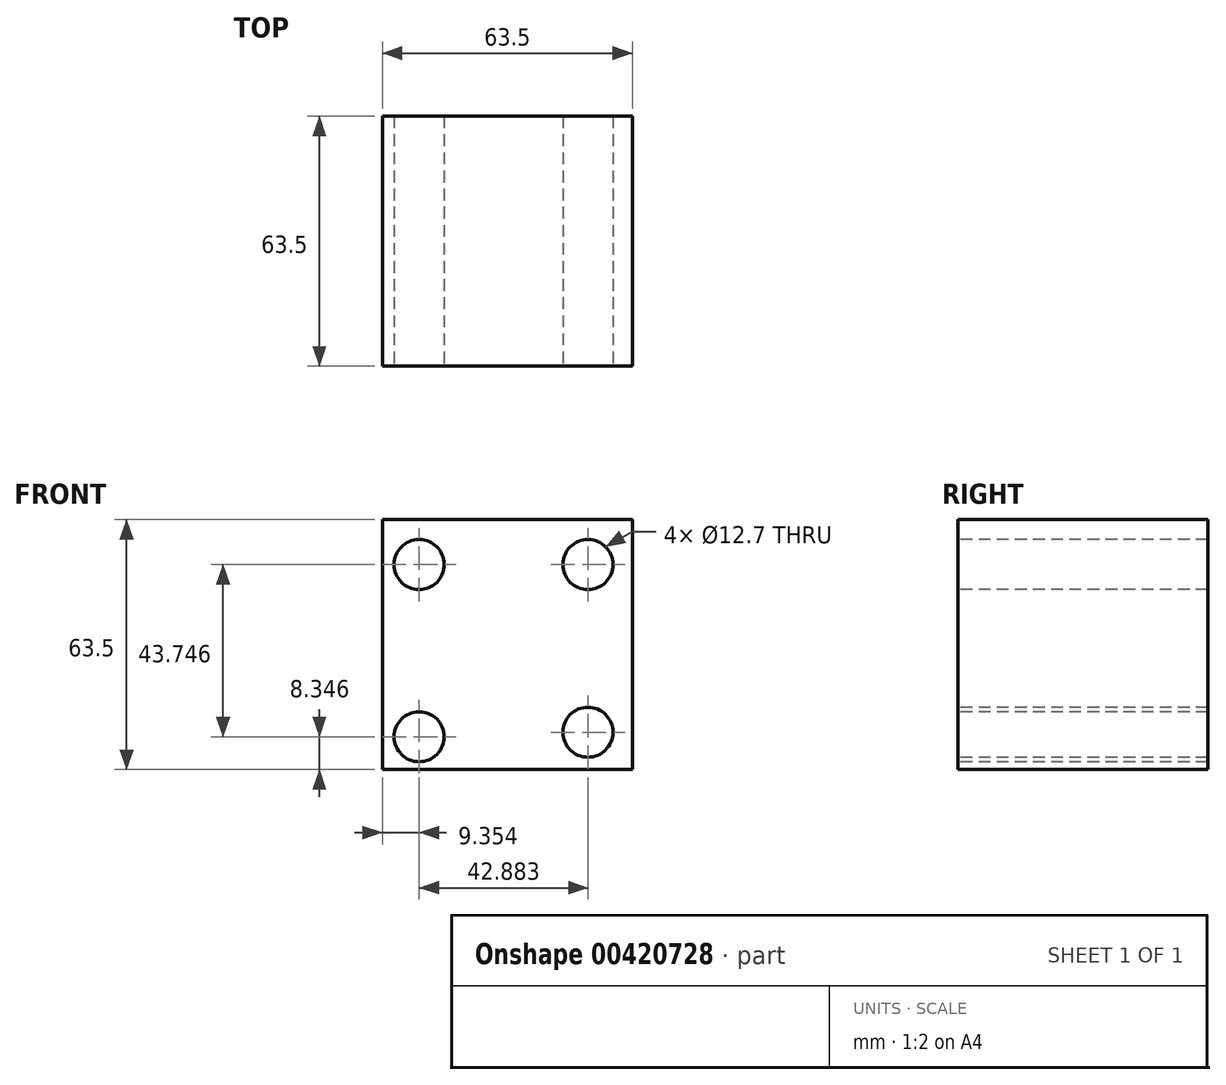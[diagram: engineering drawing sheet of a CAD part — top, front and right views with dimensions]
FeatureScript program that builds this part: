
annotation { "Feature Type Name" : "Feature", "Feature Type Description" : "" }
export const myFeature = defineFeature(function(context is Context, id is Id, definition is map)
    precondition{}
    {
        {
            var Q0;
            Q0=qCreatedBy(makeId("Front.planeOp"),FACE);
            var sketch = newSketch(context, id + "F0", { "sketchPlane" : qUnion([Q0])});
            skLineSegment(sketch, "E0.bottom", {"start": v(0, 0) * mm, "end": v(63.5, 0) * mm});
            skLineSegment(sketch, "E0.top", {"start": v(0, 63.5) * mm, "end": v(63.5, 63.5) * mm});
            skLineSegment(sketch, "E0.left", {"start": v(0, 0) * mm, "end": v(0, 63.5) * mm});
            skLineSegment(sketch, "E0.right", {"start": v(63.5, 0) * mm, "end": v(63.5, 63.5) * mm});
            skSolve(sketch);
        }
        {
            var Q0;
            Q0=qSketchRegion(id+"F0",true);
            extrude(context, id + "F1", {"entities" : qUnion([Q0]), "depth" : 63.5 * mm});
        }
        {
            var Q0;
            Q0=qCreatedBy(makeId("Front.planeOp"),FACE);
            var sketch = newSketch(context, id + "F2", { "sketchPlane" : qUnion([Q0])});
            skPoint(sketch, "E1", {"position": v(9.35, 52.1) * mm});
            skPoint(sketch, "E2", {"position": v(52.24, 52.1) * mm});
            skPoint(sketch, "E3", {"position": v(52.24, 9.5) * mm});
            skPoint(sketch, "E4", {"position": v(9.35, 8.35) * mm});
            skSolve(sketch);
        }
        {
            var Q0;
            Q0=sQuery(id+"F2.wireOp",VERTEX,"E1");
            var Q1;
            Q1=sQuery(id+"F2.wireOp",VERTEX,"E2");
            var Q2;
            Q2=sQuery(id+"F2.wireOp",VERTEX,"E3");
            var Q3;
            Q3=sQuery(id+"F2.wireOp",VERTEX,"E4");
            var Q4;
            Q4=makeQuery(id+"F1.opExtrude","SWEPT_BODY",BODY,{"disambiguationData":[OSD([sQuery(id+"F0.wireOp",EDGE,"E0.bottom"),sQuery(id+"F0.wireOp",EDGE,"E0.top"),sQuery(id+"F0.wireOp",EDGE,"E0.left"),sQuery(id+"F0.wireOp",EDGE,"E0.right")])]});
            hole(context, id + "F3", {"style" : HoleStyle.SIMPLE, "endStyle" : HoleEndStyle.THROUGH, "oppositeDirection" : true, "holeDiameter" : 12.7 * mm, "isTappedThrough" : true, "tappedDepth" : 12.7 * mm, "tapClearance" : 3, "startFromSketch" : true, "locations" : qUnion([Q0, Q1, Q2, Q3]), "scope" : qUnion([Q4])});
        }
    });
